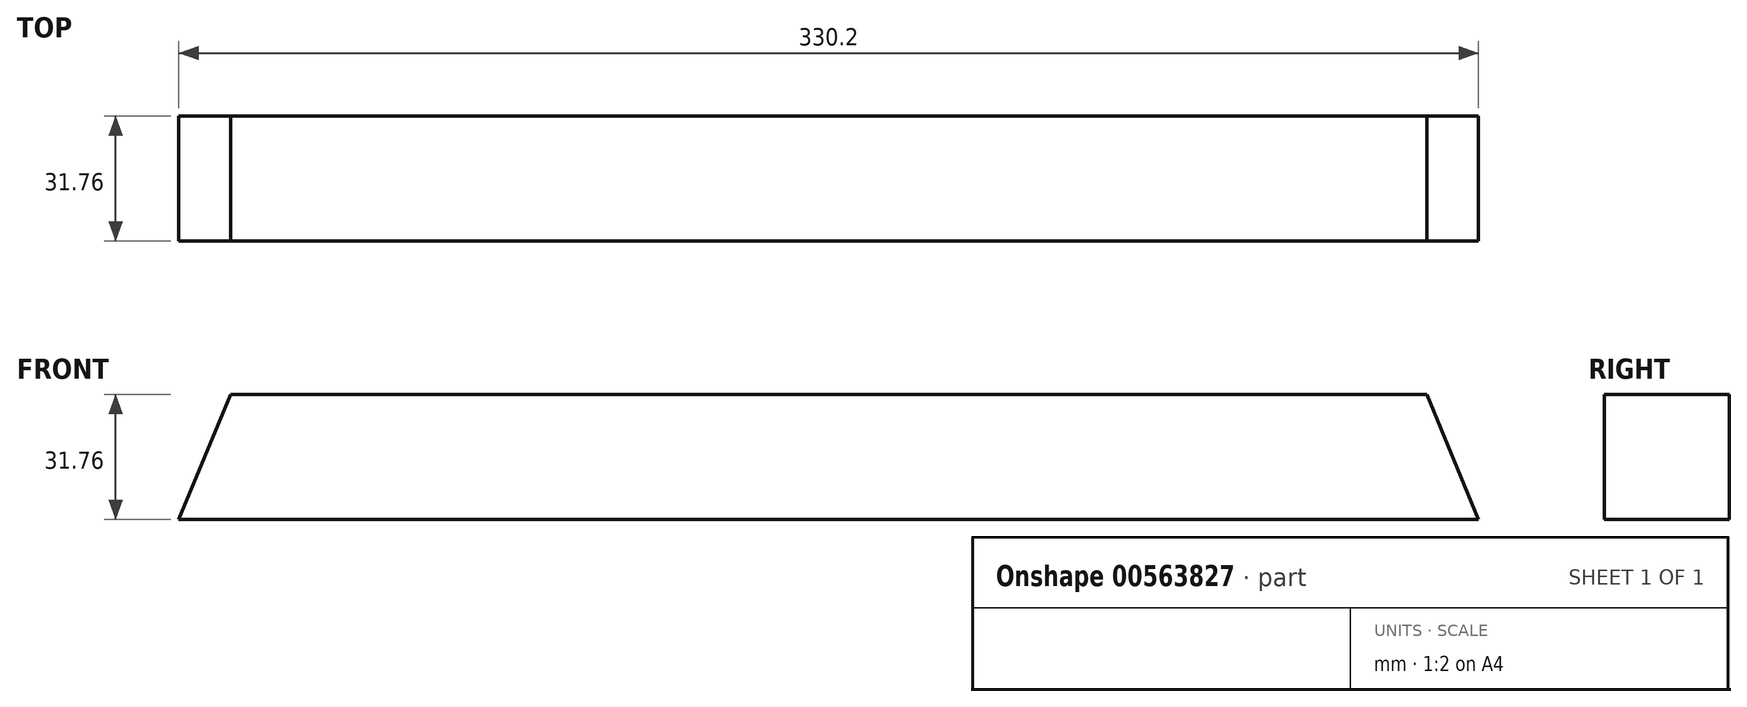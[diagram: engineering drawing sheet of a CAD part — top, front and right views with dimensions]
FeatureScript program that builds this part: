
annotation { "Feature Type Name" : "Feature", "Feature Type Description" : "" }
export const myFeature = defineFeature(function(context is Context, id is Id, definition is map)
    precondition{}
    {
        {
            var Q0;
            Q0=qCreatedBy(makeId("Front.planeOp"),FACE);
            var sketch = newSketch(context, id + "F0", { "sketchPlane" : qUnion([Q0])});
            skLineSegment(sketch, "E0.bottom", {"start": v(-165.1, 15.88) * mm, "end": v(165.1, 15.88) * mm});
            skLineSegment(sketch, "E0.top", {"start": v(-165.1, -15.87) * mm, "end": v(165.1, -15.87) * mm});
            skLineSegment(sketch, "E0.left", {"start": v(-165.1, 15.88) * mm, "end": v(-165.1, -15.87) * mm});
            skLineSegment(sketch, "E0.right", {"start": v(165.1, 15.88) * mm, "end": v(165.1, -15.87) * mm});
            skPoint(sketch, "E0.middle", {"position": v(0, 0) * mm});
            skLineSegment(sketch, "E1", {"start": v(-165.1, -15.87) * mm, "end": v(-151.95, 15.88) * mm});
            skLineSegment(sketch, "E2", {"start": v(165.1, -15.87) * mm, "end": v(151.95, 15.88) * mm});
            skSolve(sketch);
        }
        {
            var Q0;
            Q0=makeQuery(id+"F0.imprint","IMPRINT",FACE,{"disambiguationData":[TD([[makeQuery(id+"F0.imprint","IMPRINT",EDGE,{"derivedFrom":sQuery(id+"F0.wireOp",EDGE,"E0.top")}),1.0]])]});
            extrude(context, id + "F1", {"entities" : qUnion([Q0]), "endBound" : BoundingType.SYMMETRIC, "depth" : 31.75 * mm, "offsetDistance" : 25.4 * mm});
        }
    });
